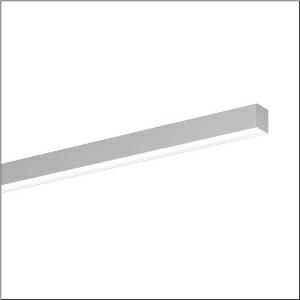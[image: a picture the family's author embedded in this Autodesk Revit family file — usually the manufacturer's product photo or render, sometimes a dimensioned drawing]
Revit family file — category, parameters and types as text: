
# Revit family: silica_r__21_51mx20dc35sb_d3c3
name_source: partatom
category: Lighting Fixtures
units: mm (PartAtom-declared; Revit-internal decimal feet)

## family parameters
Cut with Voids When Loaded = No
Host = Face
Light Source = No
Part Type = Normal
Room Calculation Point = No
Round Connector Dimension = Use Diameter
Shared = No

## types (1)
- --- (1 x LED, 6000 lm, 42.6 W, 3000K)
    Apparent Load = 43 VA
    CIE Flux Codes = 48 79 96 100 100
    Color Rendering = 80
    Color Temperature = 3000K
    Default Elevation = 1800 mm
    Description = Silica® 21, office luminaire, primary optical cover: cover, of PMMA, opal, light emission: direct distribution, primary light characteristic: symmetric, installation type: surface-mounted, LED, rated luminous flux: 6.000lm, luminous efficacy: 141lm/W, light colour: 830, colour temperature: 3000K, control gear: DALI 2, with terminal, 3+2-pole, max. 2.5mm², mains connection: 220..240V, AC, 50/60Hz, rated input power: 42.6W, luminaire housing, of aluminium, metallic grey (RAL 9006), length: 3.004mm, width: 53mm, height: 53mm, protection rating (complete): IP20, insulation class (complete): insulation class I (protective earthing), certification: CE, permissible operating ambient temperature: 0..+35°C, standard: EN 50419, packaging unit: 1 piece
    Height = 53 mm
    Lamp = 1 x LED
    Lamp Light Flux = 6000 lm
    Lamp Power = 42.6 W
    Lamp count = 1
    Length = 3004 mm
    Luminous efficacy = 141 lm/W
    Manufacturer = Siteco
    ModVariant = No
    Model = 51MX20DC35SB
    Mounting Place = Ceiling
    Mounting Type = Surface mounted
    Number of Poles = 1
    OnlyDefault = Yes
    Power Factor = 1
    Product Name = Silica® 21
    Product group = office luminaire | ceiling mounted
    ProductGroupID = 301
    Protection Class = Protection class I
    Protection Degree = IP 20
    RLX_Detail_Level = 1
    RLX_Emergency_Light_Flux = 0 lm
    RLX_Emergency_Type = 0
    RLX_Emergency_Type_DB = No
    RlxData = <blob elided: 26449 chars, md5=99874f6f>
    Socket = socket
    Standby Power = 0 W
    System Light Flux = 6000 lm
    System Power = 43 W
    Type Comments = factory setting: luminous flux: 100 % | dim-lin: 254 | 233 mA
    Type Image = l_1335933.jpg
    URL = http://relux.com
    VarID = @adj_115114
    Voltage = 0 V
    Weight = 0.00 kg
    Width = 53 mm

## geometry (parser evidence)
native form markers: Blend x4, Sweep x11
no freeform markers — native parametric forms only
